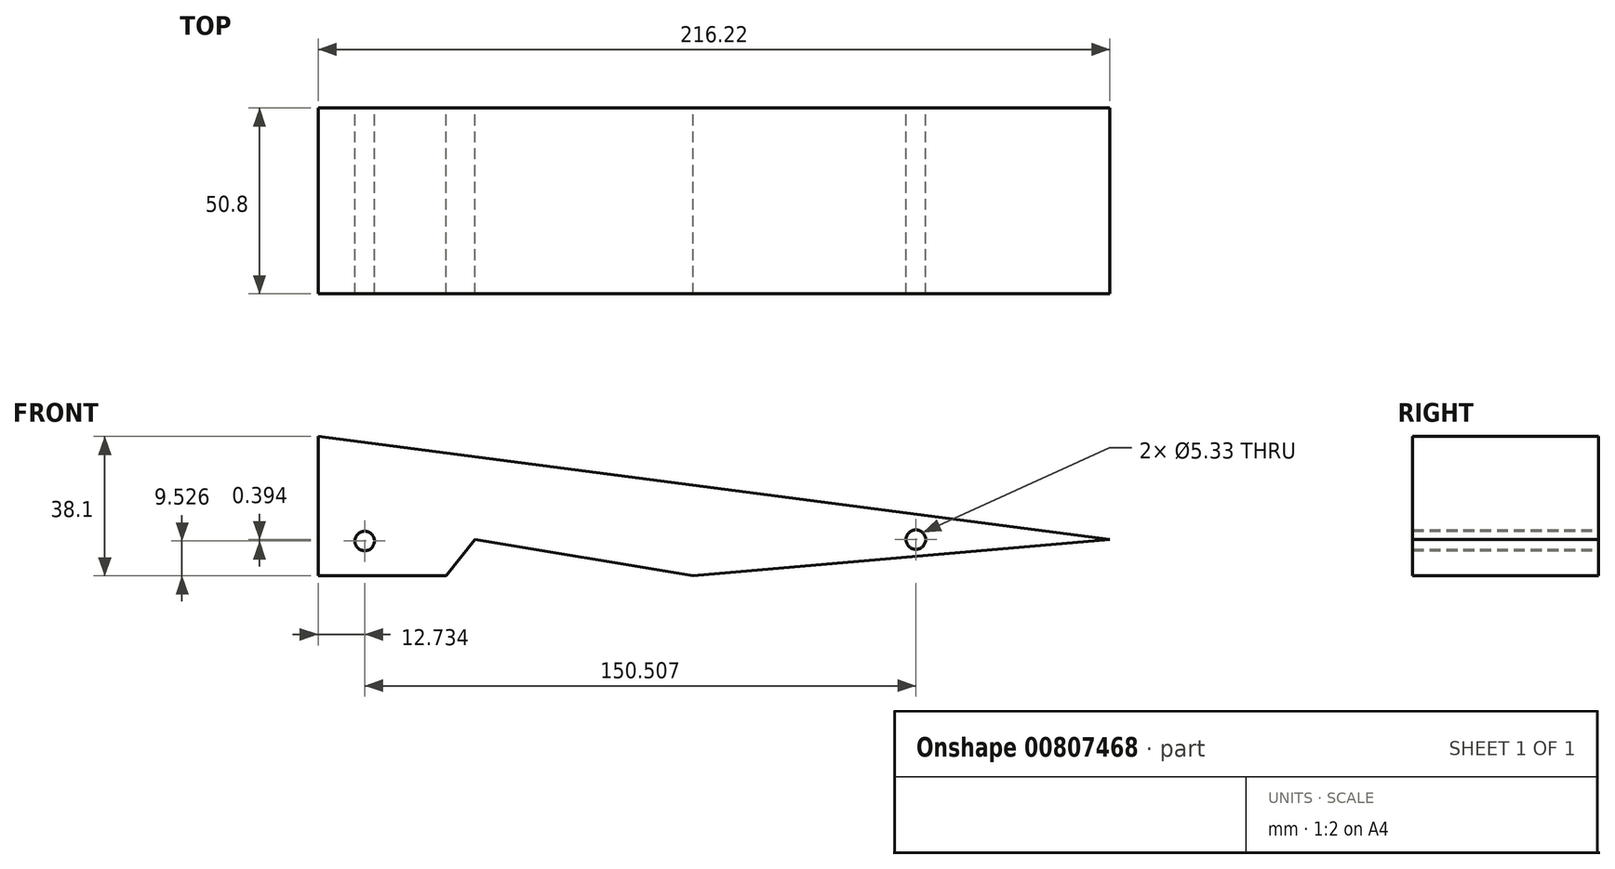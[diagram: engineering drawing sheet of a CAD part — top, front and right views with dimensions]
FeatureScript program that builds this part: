
annotation { "Feature Type Name" : "Feature", "Feature Type Description" : "" }
export const myFeature = defineFeature(function(context is Context, id is Id, definition is map)
    precondition{}
    {
        {
            var Q0;
            Q0=qCreatedBy(makeId("Front.planeOp"),FACE);
            var sketch = newSketch(context, id + "F0", { "sketchPlane" : qUnion([Q0])});
            skLineSegment(sketch, "E0", {"start": v(-55.8, 28.18) * mm, "end": v(-55.8, -9.92) * mm});
            skLineSegment(sketch, "E1", {"start": v(-55.8, -9.92) * mm, "end": v(-20.87, -9.92) * mm});
            skLineSegment(sketch, "E2", {"start": v(-20.87, -9.92) * mm, "end": v(-12.95, 0) * mm});
            skLineSegment(sketch, "E3", {"start": v(-12.95, 0) * mm, "end": v(46.55, -9.92) * mm});
            skLineSegment(sketch, "E4", {"start": v(46.55, -9.92) * mm, "end": v(160.42, 0) * mm});
            skLineSegment(sketch, "E5", {"start": v(-55.8, 28.18) * mm, "end": v(160.42, 0) * mm});
            skCircle(sketch, "E6", {"center": v(-43.07, -0.4) * mm, "radius": 2.67 * mm});
            skCircle(sketch, "E7", {"center": v(107.44, 0) * mm, "radius": 2.67 * mm});
            skSolve(sketch);
        }
        {
            var Q0;
            Q0=makeQuery(id+"F0.imprint","IMPRINT",FACE,{"disambiguationData":[TD([[makeQuery(id+"F0.imprint","IMPRINT",EDGE,{"derivedFrom":sQuery(id+"F0.wireOp",EDGE,"E0")}),1.0]])]});
            extrude(context, id + "F1", {"entities" : qUnion([Q0]), "depth" : 25.4 * mm, "offsetDistance" : 25.4 * mm, "hasSecondDirection" : true, "secondDirectionOppositeDirection" : true, "secondDirectionDepth" : 25.4 * mm});
        }
    });
